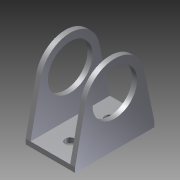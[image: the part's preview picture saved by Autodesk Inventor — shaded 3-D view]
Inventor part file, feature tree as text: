
AUTODESK INVENTOR PART (.ipt)
format: ipt  version: 2012 (Build 160160000, 160)  size: 130,048 bytes
history: native  units: in
note: dims shown in document units (in); Inventor stores cm internally (conversion verified against a paired STEP export)
features: extrude x3, sketch x3
ambient origin geometry x8: Origin, YZ Plane, XZ Plane, XY Plane, X Axis, Y Axis, Z Axis, Center Point
bodies: Solid1 (feature_tree)
feature tree (6):
  extrude  "Extrusion1"  Depth=1.25in
  extrude  "Extrusion2"  Depth=0.125in
  extrude  "Extrusion3"  Depth=2.0in TaperAngle=0.0deg
  sketch  "Sketch1"  dims[d0=2.0in d1=1.25in]
  sketch  "Sketch2"  dims[d2=0.125in d3=0.125in]
  sketch  "Sketch3"  dims[d4=0.125in d5=2.0in d6=0.0in d7=1.125in d8=1.0in d9=0.75in d10=2.0in d11=0.0in d12=0.25in d13=0.25in d14=0.5in d15=0.5in d16=0.5in d17=0.5in d18=2.0in d19=0.0in d20=1.0in]
